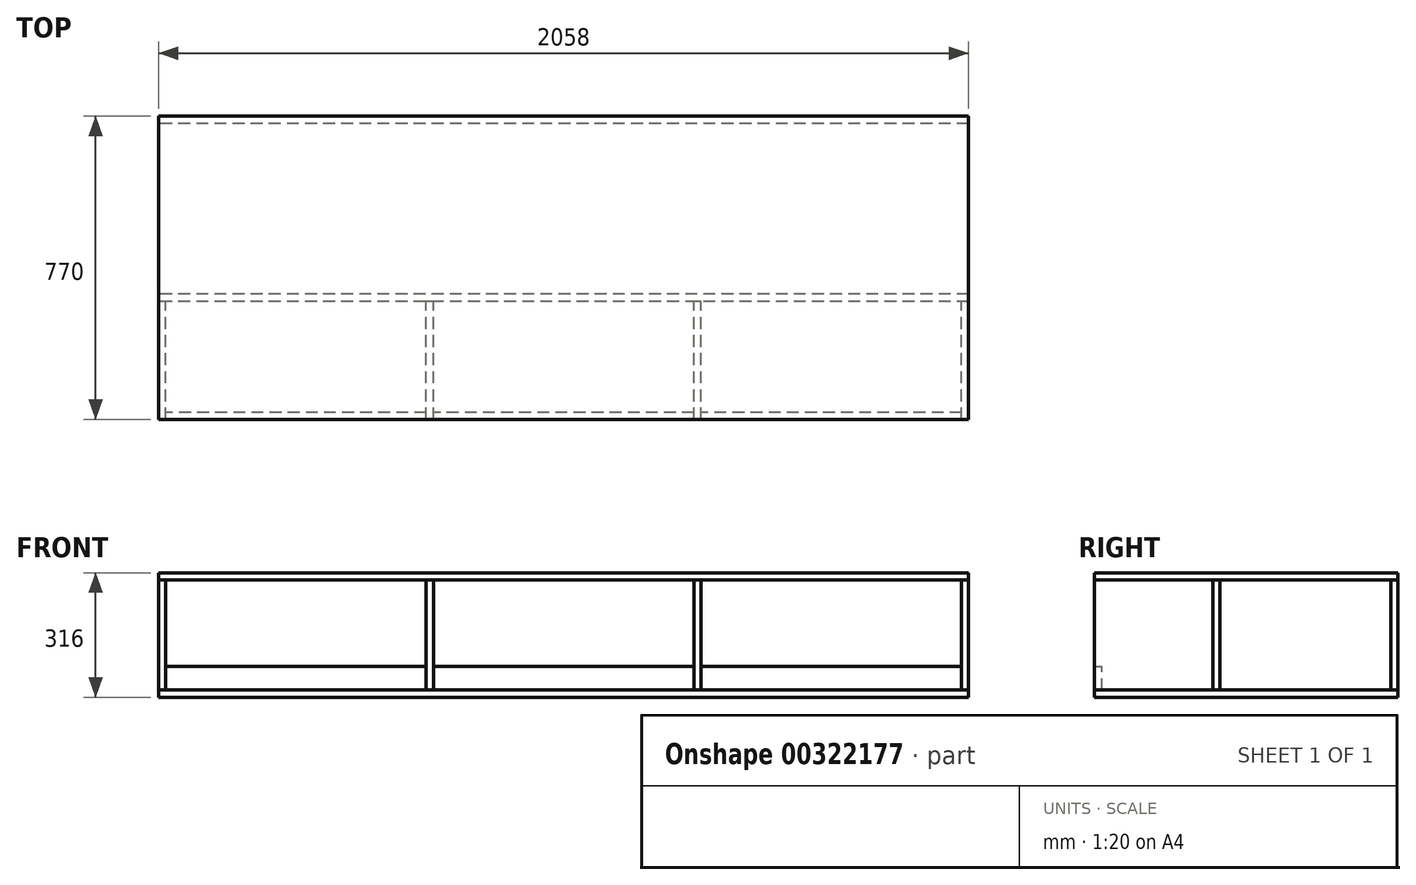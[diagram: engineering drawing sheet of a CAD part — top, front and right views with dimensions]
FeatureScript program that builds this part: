
annotation { "Feature Type Name" : "Feature", "Feature Type Description" : "" }
export const myFeature = defineFeature(function(context is Context, id is Id, definition is map)
    precondition{}
    {
        {
            var Q0;
            Q0=qCreatedBy(makeId("Right.planeOp"),FACE);
            var sketch = newSketch(context, id + "F0", { "sketchPlane" : qUnion([Q0])});
            skLineSegment(sketch, "E0.bottom", {"start": v(-150, 143.45) * mm, "end": v(150, 143.45) * mm});
            skLineSegment(sketch, "E0.top", {"start": v(-150, -136.55) * mm, "end": v(150, -136.55) * mm});
            skLineSegment(sketch, "E0.left", {"start": v(-150, 143.45) * mm, "end": v(-150, -136.55) * mm});
            skLineSegment(sketch, "E0.right", {"start": v(150, 143.45) * mm, "end": v(150, -136.55) * mm});
            skPoint(sketch, "E0.middle", {"position": v(0, 3.45) * mm});
            skSolve(sketch);
        }
        {
            var Q0;
            Q0 = qSketchRegion(id + "F0", true);
            extrude(context, id + "F1", {"entities" : qUnion([Q0]), "depth" : 18 * mm});
        }
        {
            var Q0;
            Q0=makeQuery(id+"F1.opExtrude","SWEPT_BODY",BODY,{"disambiguationData":[OSD([sQuery(id+"F0.wireOp",EDGE,"E0.bottom"),sQuery(id+"F0.wireOp",EDGE,"E0.top"),sQuery(id+"F0.wireOp",EDGE,"E0.left"),sQuery(id+"F0.wireOp",EDGE,"E0.right")])]});
            transform(context, id + "F2", {"entities" : qUnion([Q0]), "transformType" : TransformType.TRANSLATION_3D, "dx" : 680 * mm, "dy" : 0 * mm, "dz" : 0 * mm, "makeCopy" : true});
        }
        {
            var Q0;
            Q0=makeQuery(id+"F2.opPattern","COPY",BODY,{"derivedFrom":makeQuery(id+"F1.opExtrude","SWEPT_BODY",BODY,{"disambiguationData":[OSD([sQuery(id+"F0.wireOp",EDGE,"E0.bottom"),sQuery(id+"F0.wireOp",EDGE,"E0.top"),sQuery(id+"F0.wireOp",EDGE,"E0.left"),sQuery(id+"F0.wireOp",EDGE,"E0.right")])]}),"instanceName":"1"});
            transform(context, id + "F3", {"entities" : qUnion([Q0]), "transformType" : TransformType.TRANSLATION_3D, "dx" : 680 * mm, "dy" : 0 * mm, "dz" : 0 * mm, "makeCopy" : true});
        }
        {
            var Q0;
            Q0=makeQuery(id+"F3.opPattern","COPY",BODY,{"derivedFrom":makeQuery(id+"F2.opPattern","COPY",BODY,{"derivedFrom":makeQuery(id+"F1.opExtrude","SWEPT_BODY",BODY,{"disambiguationData":[OSD([sQuery(id+"F0.wireOp",EDGE,"E0.bottom"),sQuery(id+"F0.wireOp",EDGE,"E0.top"),sQuery(id+"F0.wireOp",EDGE,"E0.left"),sQuery(id+"F0.wireOp",EDGE,"E0.right")])]}),"instanceName":"1"}),"instanceName":"1"});
            transform(context, id + "F4", {"entities" : qUnion([Q0]), "transformType" : TransformType.TRANSLATION_3D, "dx" : 680 * mm, "dy" : 0 * mm, "dz" : 0 * mm, "makeCopy" : true});
        }
        {
            var Q0;
            Q0=makeQuery(id+"F4.opPattern","COPY",FACE,{"derivedFrom":makeQuery(id+"F3.opPattern","COPY",FACE,{"derivedFrom":makeQuery(id+"F2.opPattern","COPY",FACE,{"derivedFrom":makeQuery(id+"F1.opExtrude","SWEPT_FACE",FACE,{"disambiguationData":[OSD([sQuery(id+"F0.wireOp",EDGE,"E0.top")])]}),"instanceName":"1"}),"instanceName":"1"}),"instanceName":"1"});
            var sketch = newSketch(context, id + "F5", { "sketchPlane" : qUnion([Q0])});
            skLineSegment(sketch, "E1.bottom", {"start": v(2058, 150) * mm, "end": v(0, 150) * mm});
            skLineSegment(sketch, "E1.top", {"start": v(2058, -620) * mm, "end": v(0, -620) * mm});
            skLineSegment(sketch, "E1.left", {"start": v(2058, 150) * mm, "end": v(2058, -620) * mm});
            skLineSegment(sketch, "E1.right", {"start": v(0, 150) * mm, "end": v(0, -620) * mm});
            skSolve(sketch);
        }
        {
            var Q0;
            Q0 = qSketchRegion(id + "F5", true);
            extrude(context, id + "F6", {"entities" : qUnion([Q0]), "depth" : 18 * mm});
        }
        {
            var Q0;
            Q0=makeQuery(id+"F6.opExtrude","SWEPT_BODY",BODY,{"disambiguationData":[OSD([sQuery(id+"F5.wireOp",EDGE,"E1.bottom"),sQuery(id+"F5.wireOp",EDGE,"E1.top"),sQuery(id+"F5.wireOp",EDGE,"E1.left"),sQuery(id+"F5.wireOp",EDGE,"E1.right")])]});
            transform(context, id + "F7", {"entities" : qUnion([Q0]), "transformType" : TransformType.TRANSLATION_3D, "dx" : 0 * mm, "dy" : 0 * mm, "dz" : 298 * mm, "makeCopy" : true});
        }
        {
            var Q0;
            Q0=makeQuery(id+"F4.opPattern","COPY",FACE,{"derivedFrom":makeQuery(id+"F3.opPattern","COPY",FACE,{"derivedFrom":makeQuery(id+"F2.opPattern","COPY",FACE,{"derivedFrom":makeQuery(id+"F1.opExtrude","SWEPT_FACE",FACE,{"disambiguationData":[OSD([sQuery(id+"F0.wireOp",EDGE,"E0.right")])]}),"instanceName":"1"}),"instanceName":"1"}),"instanceName":"1"});
            var sketch = newSketch(context, id + "F8", { "sketchPlane" : qUnion([Q0])});
            skLineSegment(sketch, "E2.bottom", {"start": v(-2058, 143.45) * mm, "end": v(0, 143.45) * mm});
            skLineSegment(sketch, "E2.top", {"start": v(-2058, -136.55) * mm, "end": v(0, -136.55) * mm});
            skLineSegment(sketch, "E2.left", {"start": v(-2058, 143.45) * mm, "end": v(-2058, -136.55) * mm});
            skLineSegment(sketch, "E2.right", {"start": v(0, 143.45) * mm, "end": v(0, -136.55) * mm});
            skSolve(sketch);
        }
        {
            var Q0;
            Q0 = qSketchRegion(id + "F8", true);
            extrude(context, id + "F9", {"entities" : qUnion([Q0]), "depth" : 18 * mm});
        }
        {
            var Q0;
            Q0=makeQuery(id+"F9.opExtrude","SWEPT_BODY",BODY,{"disambiguationData":[OSD([sQuery(id+"F8.wireOp",EDGE,"E2.bottom"),sQuery(id+"F8.wireOp",EDGE,"E2.top"),sQuery(id+"F8.wireOp",EDGE,"E2.left"),sQuery(id+"F8.wireOp",EDGE,"E2.right")])]});
            transform(context, id + "F10", {"entities" : qUnion([Q0]), "transformType" : TransformType.TRANSLATION_3D, "dx" : 0 * mm, "dy" : 452 * mm, "dz" : 0 * mm, "makeCopy" : true});
        }
        {
            var Q0;
            Q0=makeQuery(id+"F1.opExtrude","CAP_FACE",FACE,{"disambiguationData":[OSD([sQuery(id+"F0.wireOp",EDGE,"E0.bottom"),sQuery(id+"F0.wireOp",EDGE,"E0.top"),sQuery(id+"F0.wireOp",EDGE,"E0.left"),sQuery(id+"F0.wireOp",EDGE,"E0.right")])],"isStart":false});
            var sketch = newSketch(context, id + "F11", { "sketchPlane" : qUnion([Q0])});
            skLineSegment(sketch, "E3.bottom", {"start": v(-150, -136.55) * mm, "end": v(-132, -136.55) * mm});
            skLineSegment(sketch, "E3.top", {"start": v(-150, -76.55) * mm, "end": v(-132, -76.55) * mm});
            skLineSegment(sketch, "E3.left", {"start": v(-150, -136.55) * mm, "end": v(-150, -76.55) * mm});
            skLineSegment(sketch, "E3.right", {"start": v(-132, -136.55) * mm, "end": v(-132, -76.55) * mm});
            skSolve(sketch);
        }
        {
            var Q0;
            Q0 = qSketchRegion(id + "F11", true);
            var Q1;
            Q1=makeQuery(id+"F2.opPattern","COPY",FACE,{"derivedFrom":makeQuery(id+"F1.opExtrude","CAP_FACE",FACE,{"disambiguationData":[OSD([sQuery(id+"F0.wireOp",EDGE,"E0.bottom"),sQuery(id+"F0.wireOp",EDGE,"E0.top"),sQuery(id+"F0.wireOp",EDGE,"E0.left"),sQuery(id+"F0.wireOp",EDGE,"E0.right")])],"isStart":true}),"instanceName":"1"});
            extrude(context, id + "F12", {"entities" : qUnion([Q0]), "endBound" : BoundingType.UP_TO_SURFACE, "endBoundEntityFace" : qUnion([Q1]), "depth" : 25 * mm});
        }
        {
            var Q0;
            Q0=makeQuery(id+"F12.opExtrude","SWEPT_BODY",BODY,{"disambiguationData":[OSD([sQuery(id+"F11.wireOp",EDGE,"E3.bottom"),sQuery(id+"F11.wireOp",EDGE,"E3.top"),sQuery(id+"F11.wireOp",EDGE,"E3.left"),sQuery(id+"F11.wireOp",EDGE,"E3.right")])]});
            transform(context, id + "F13", {"entities" : qUnion([Q0]), "transformType" : TransformType.TRANSLATION_3D, "dx" : 680 * mm, "dy" : 0 * mm, "dz" : 0 * mm, "makeCopy" : true});
        }
        {
            var Q0;
            Q0=makeQuery(id+"F13.opPattern","COPY",BODY,{"derivedFrom":makeQuery(id+"F12.opExtrude","SWEPT_BODY",BODY,{"disambiguationData":[OSD([sQuery(id+"F11.wireOp",EDGE,"E3.bottom"),sQuery(id+"F11.wireOp",EDGE,"E3.top"),sQuery(id+"F11.wireOp",EDGE,"E3.left"),sQuery(id+"F11.wireOp",EDGE,"E3.right")])]}),"instanceName":"1"});
            transform(context, id + "F14", {"entities" : qUnion([Q0]), "transformType" : TransformType.TRANSLATION_3D, "dx" : 680 * mm, "dy" : 0 * mm, "dz" : 0 * mm, "makeCopy" : true});
        }
    });
